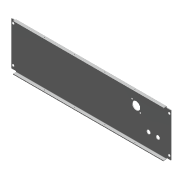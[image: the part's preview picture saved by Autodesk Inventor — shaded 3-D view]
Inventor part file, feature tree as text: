
AUTODESK INVENTOR PART (.ipt)
format: ipt  version: 2016 SP2 (Build 200236200, 236)  size: 176,640 bytes
history: native  units: in
note: dims shown in document units (in); Inventor stores cm internally (conversion verified against a paired STEP export)
features: sketch x2, hole x1, extrude x1
ambient origin geometry x8: Origin, YZ Plane, XZ Plane, XY Plane, X Axis, Y Axis, Z Axis, Center Point
bodies: Solid1 (feature_tree)
feature tree (4):
  hole  "Hole1"  [1 undecoded]
  extrude  "Extrusion1"  Depth=0.4331in
  sketch  "Sketch1"  dims[d0=0.4134in d1=0.2362in d2=0.1575in d3=0.0787in d4=90.0deg d5=0.315in d6=0.8108in d7=0.8465in]
  sketch  "Sketch2"  dims[d8=0.1575in d9=0.4331in d10=0.4331in d11=0.4331in d12=0.4331in d13=1.2249in d14=0.3937in d15=0.0in d16=4.4094in d18=2.1654in d19=2.1654in d20=3.0315in d21=1.1811in d22=5.1181in]
note: 1 required parameter value undecoded (feature->parameter linkage not recoverable at this tier; creation-order binding heuristic only, values carry confidence <= 0.55)
